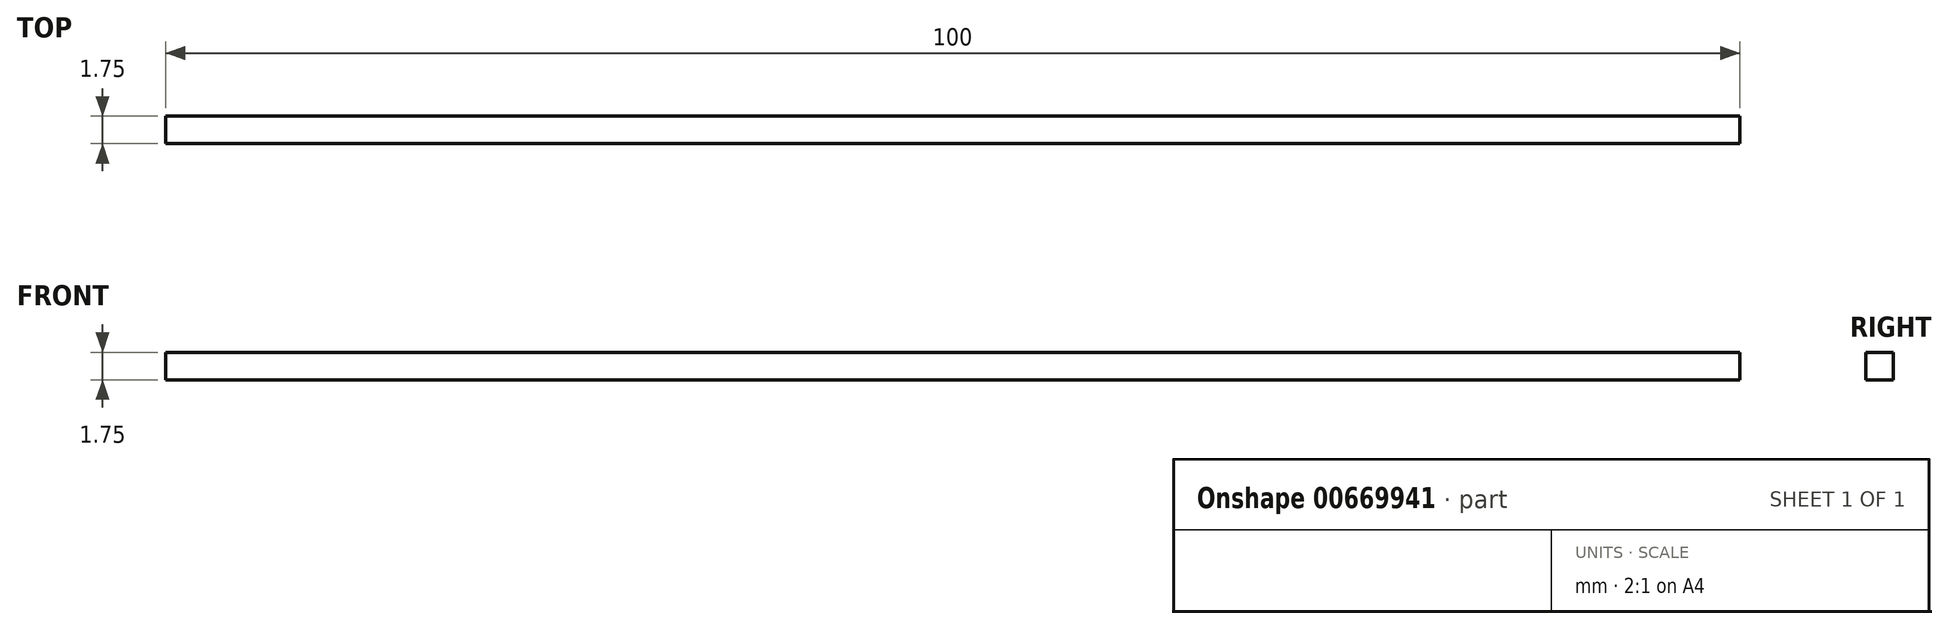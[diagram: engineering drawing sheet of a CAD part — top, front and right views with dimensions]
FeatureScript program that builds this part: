
annotation { "Feature Type Name" : "Feature", "Feature Type Description" : "" }
export const myFeature = defineFeature(function(context is Context, id is Id, definition is map)
    precondition{}
    {
        {
            var Q0;
            Q0=qCreatedBy(makeId("Top.planeOp"),FACE);
            var sketch = newSketch(context, id + "F0", { "sketchPlane" : qUnion([Q0])});
            skLineSegment(sketch, "E0", {"start": v(-62.48, 29.87) * mm, "end": v(37.52, 29.87) * mm});
            skLineSegment(sketch, "E1", {"start": v(-62.48, 29.87) * mm, "end": v(-62.48, 28.12) * mm});
            skLineSegment(sketch, "E2", {"start": v(-62.48, 28.12) * mm, "end": v(37.52, 28.12) * mm});
            skLineSegment(sketch, "E3", {"start": v(37.52, 28.12) * mm, "end": v(37.52, 29.87) * mm});
            skSolve(sketch);
        }
        {
            var Q0;
            Q0=makeQuery(id+"F0.imprint","IMPRINT",FACE,{"disambiguationData":[TD([[makeQuery(id+"F0.imprint","IMPRINT",EDGE,{"derivedFrom":sQuery(id+"F0.wireOp",EDGE,"E0")}),-1.0]])]});
            extrude(context, id + "F1", {"entities" : qUnion([Q0]), "depth" : 1.75 * mm, "offsetDistance" : 25.4 * mm});
        }
    });
